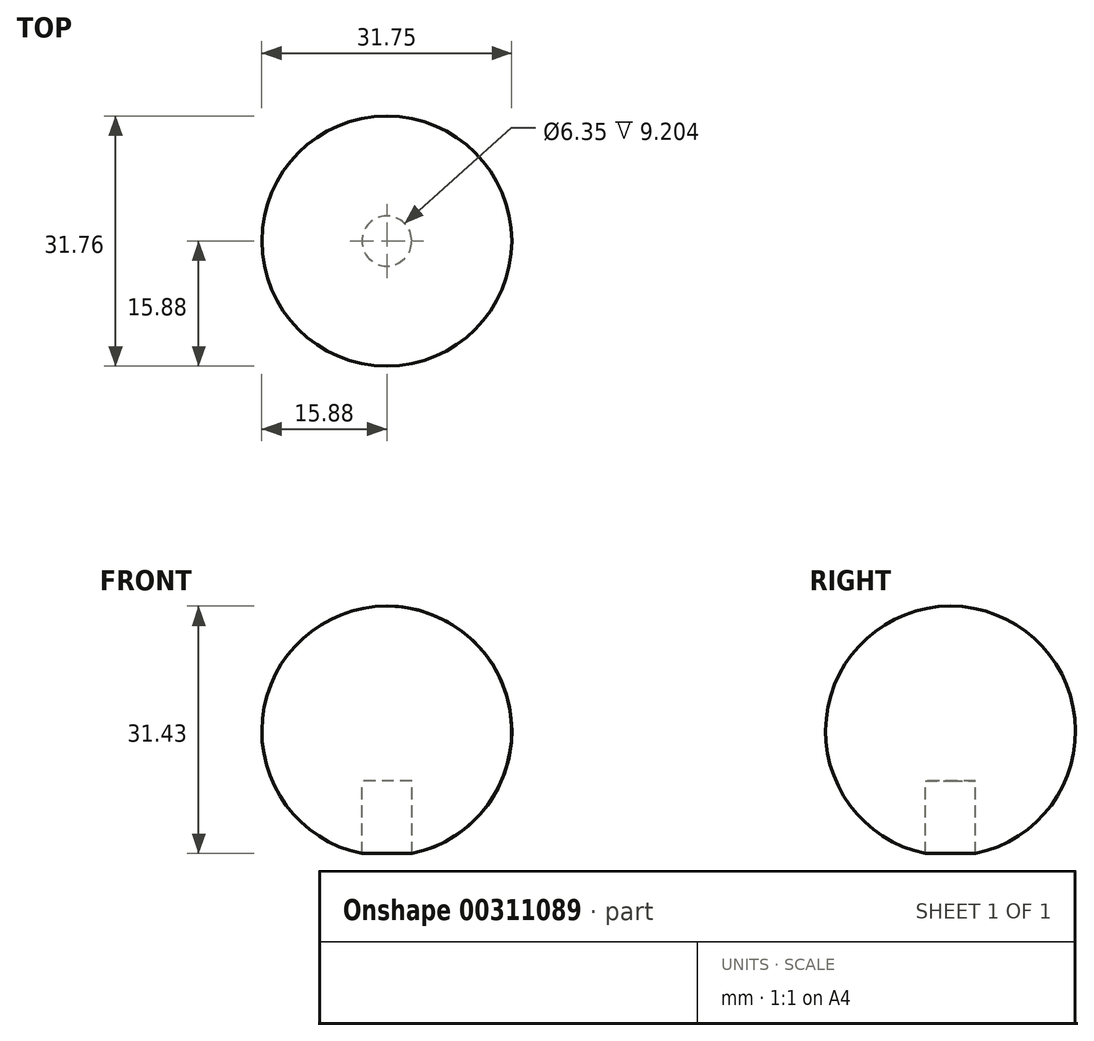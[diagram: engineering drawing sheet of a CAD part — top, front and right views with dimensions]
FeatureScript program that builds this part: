
annotation { "Feature Type Name" : "Feature", "Feature Type Description" : "" }
export const myFeature = defineFeature(function(context is Context, id is Id, definition is map)
    precondition{}
    {
        {
            var Q0;
            Q0=qCreatedBy(makeId("Front.planeOp"),FACE);
            var sketch = newSketch(context, id + "F0", { "sketchPlane" : qUnion([Q0])});
            skArc(sketch, "E0", {"start": v(0, 15.88) * mm, "mid": v(-15.88, 0) * mm, "end": v(0, -15.88) * mm});
            skLineSegment(sketch, "E1", {"start": v(0, 15.88) * mm, "end": v(0, -15.88) * mm});
            skSolve(sketch);
        }
        {
            var Q0;
            Q0=qCreatedBy(makeId("Top.planeOp"),FACE);
            var sketch = newSketch(context, id + "F1", { "sketchPlane" : qUnion([Q0])});
            skCircle(sketch, "E2", {"center": v(0, 0) * mm, "radius": 15.88 * mm});
            skSolve(sketch);
        }
        {
            var Q0;
            Q0=makeQuery(id+"F0.imprint","IMPRINT",FACE,{"disambiguationData":[TD([[makeQuery(id+"F0.imprint","IMPRINT",EDGE,{"derivedFrom":sQuery(id+"F0.wireOp",EDGE,"E0")}),1.0]])]});
            var Q1;
            Q1=sQuery(id+"F1.wireOp",EDGE,"E2");
            revolve(context, id + "F2", {"entities" : qUnion([Q0]), "axis" : qUnion([Q1]), "revolveType" : RevolveType.FULL});
        }
        {
            var Q0;
            Q0=qCreatedBy(makeId("Top.planeOp"),FACE);
            cPlane(context, id + "F3", {"entities" : qUnion([Q0]), "cplaneType" : CPlaneType.OFFSET, "offset" : 6.35 * mm, "oppositeDirection" : true, "width" : 152.4 * mm, "height" : 152.4 * mm});
        }
        {
            var Q0;
            Q0=qCreatedBy(id+"F3.planeOp",FACE);
            var sketch = newSketch(context, id + "F4", { "sketchPlane" : qUnion([Q0])});
            skCircle(sketch, "E3", {"center": v(0, 0) * mm, "radius": 3.18 * mm});
            skSolve(sketch);
        }
        {
            var Q0;
            Q0 = qSketchRegion(id + "F4", true);
            extrude(context, id + "F5", {"entities" : qUnion([Q0]), "oppositeDirection" : true, "depth" : 25.4 * mm});
        }
        {
            var Q0;
            Q0=makeQuery(id+"F5.opExtrude","SWEPT_BODY",BODY,{"disambiguationData":[OSD([sQuery(id+"F4.wireOp",EDGE,"E3")])]});
            var Q1;
            Q1=makeQuery(id+"F2.opRevolve","SWEPT_BODY",BODY,{"disambiguationData":[OSD([sQuery(id+"F0.wireOp",EDGE,"E0"),sQuery(id+"F0.wireOp",EDGE,"E1")])]});
            booleanBodies(context, id + "F6", {"operationType" : BooleanOperationType.SUBTRACTION, "tools" : qUnion([Q0]), "targets" : qUnion([Q1])});
        }
    });
